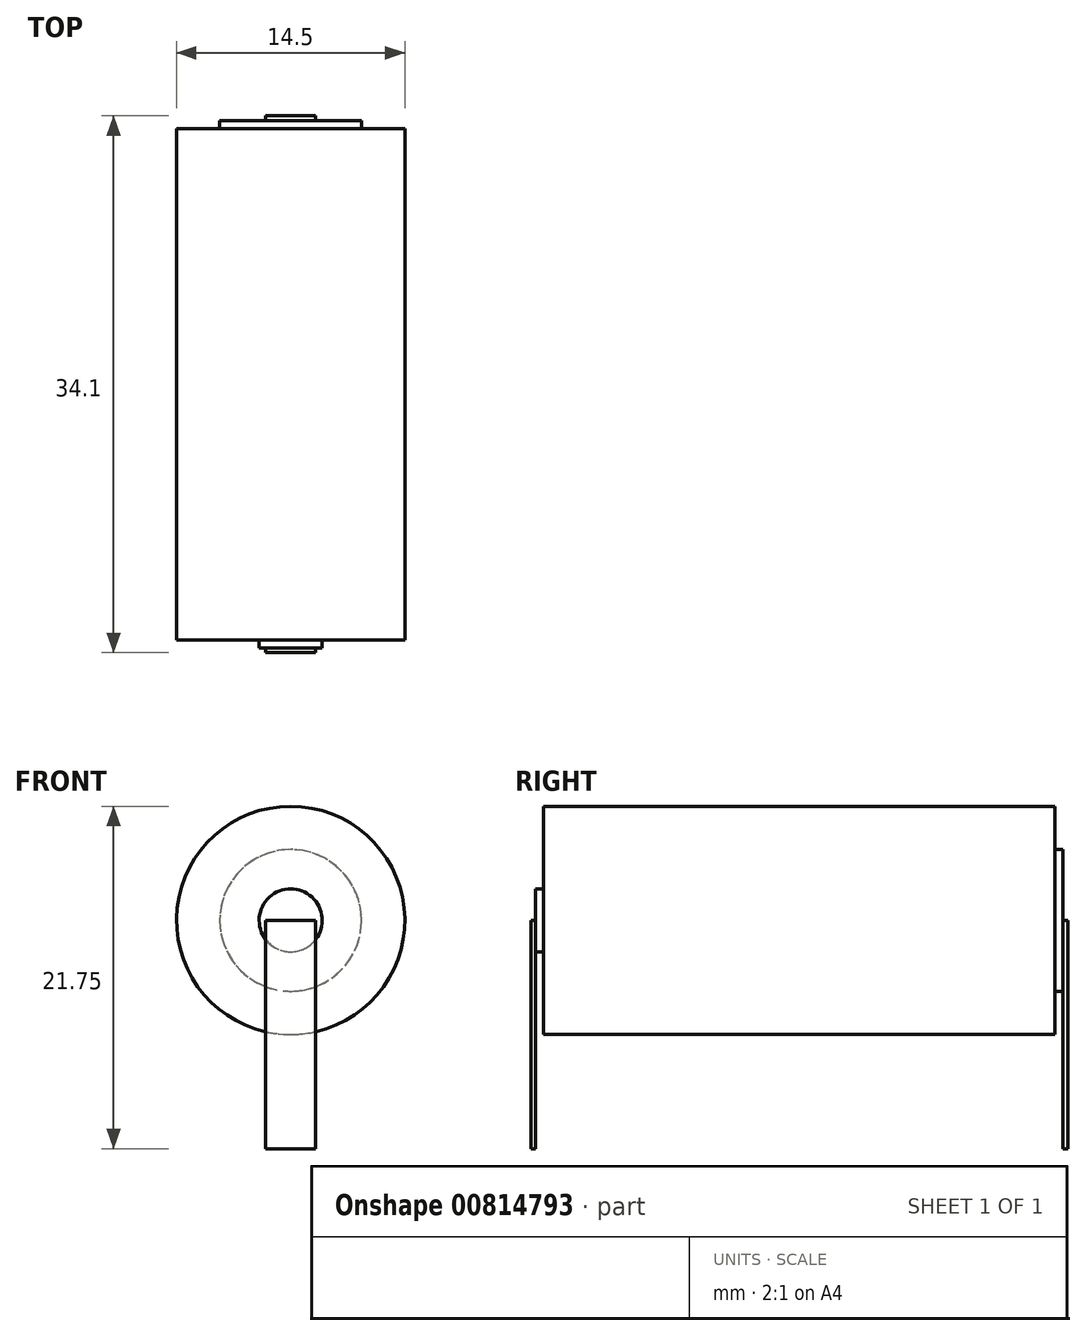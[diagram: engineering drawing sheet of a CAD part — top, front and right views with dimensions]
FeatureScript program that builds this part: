
annotation { "Feature Type Name" : "Feature", "Feature Type Description" : "" }
export const myFeature = defineFeature(function(context is Context, id is Id, definition is map)
    precondition{}
    {
        {
            var Q0;
            Q0=qCreatedBy(makeId("Front.planeOp"),FACE);
            var sketch = newSketch(context, id + "F0", { "sketchPlane" : qUnion([Q0])});
            skCircle(sketch, "E0", {"center": v(0, 0) * mm, "radius": 7.25 * mm});
            skSolve(sketch);
        }
        {
            var Q0;
            Q0 = qSketchRegion(id + "F0", true);
            extrude(context, id + "F1", {"entities" : qUnion([Q0]), "depth" : 32.5 * mm, "offsetDistance" : 25 * mm});
        }
        {
            var Q0;
            Q0=qCreatedBy(makeId("Front.planeOp"),FACE);
            var sketch = newSketch(context, id + "F2", { "sketchPlane" : qUnion([Q0])});
            skCircle(sketch, "E1", {"center": v(0, 0) * mm, "radius": 4.5 * mm});
            skSolve(sketch);
        }
        {
            var Q0;
            Q0 = qSketchRegion(id + "F2", true);
            extrude(context, id + "F3", {"entities" : qUnion([Q0]), "operationType" : NewBodyOperationType.ADD, "oppositeDirection" : true, "depth" : 0.5 * mm, "offsetDistance" : 25 * mm});
        }
        {
            var Q0;
            Q0=qCreatedBy(makeId("Front.planeOp"),FACE);
            cPlane(context, id + "F4", {"entities" : qUnion([Q0]), "cplaneType" : CPlaneType.OFFSET, "offset" : 32.5 * mm, "width" : 150 * mm, "height" : 150 * mm});
        }
        {
            var Q0;
            Q0=qCreatedBy(id+"F4.planeOp",FACE);
            var sketch = newSketch(context, id + "F5", { "sketchPlane" : qUnion([Q0])});
            skCircle(sketch, "E2", {"center": v(0, 0) * mm, "radius": 2 * mm});
            skSolve(sketch);
        }
        {
            var Q0;
            Q0 = qSketchRegion(id + "F5", true);
            extrude(context, id + "F6", {"entities" : qUnion([Q0]), "operationType" : NewBodyOperationType.ADD, "depth" : 0.5 * mm, "offsetDistance" : 25 * mm});
        }
        {
            var Q0;
            Q0=qCreatedBy(makeId("Top.planeOp"),FACE);
            var sketch = newSketch(context, id + "F7", { "sketchPlane" : qUnion([Q0])});
            skLineSegment(sketch, "E3", {"start": v(-1.59, 0.8) * mm, "end": v(-1.59, 0.5) * mm});
            skLineSegment(sketch, "E4", {"start": v(1.59, 0.8) * mm, "end": v(1.59, 0.5) * mm});
            skLineSegment(sketch, "E5", {"start": v(-1.59, 0.8) * mm, "end": v(1.59, 0.8) * mm});
            skLineSegment(sketch, "E6", {"start": v(-1.59, 0.5) * mm, "end": v(1.59, 0.5) * mm});
            skLineSegment(sketch, "E7.MirrorCS", {"start": v(1.59, -33.3) * mm, "end": v(1.59, -33) * mm});
            skLineSegment(sketch, "E8.MirrorCS", {"start": v(-1.59, -33.3) * mm, "end": v(-1.59, -33) * mm});
            skLineSegment(sketch, "E9.MirrorCS", {"start": v(-1.59, -33.3) * mm, "end": v(1.59, -33.3) * mm});
            skLineSegment(sketch, "E10.MirrorCS", {"start": v(-1.59, -33) * mm, "end": v(1.59, -33) * mm});
            skSolve(sketch);
        }
        {
            var Q0;
            Q0 = qSketchRegion(id + "F7", true);
            extrude(context, id + "F8", {"entities" : qUnion([Q0]), "operationType" : NewBodyOperationType.ADD, "oppositeDirection" : true, "depth" : 14.5 * mm, "offsetDistance" : 25 * mm});
        }
    });
